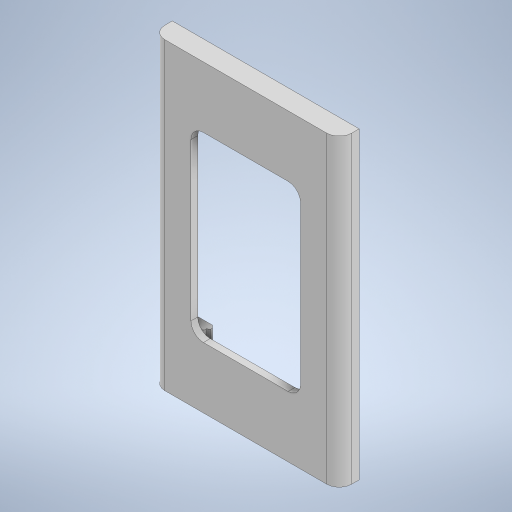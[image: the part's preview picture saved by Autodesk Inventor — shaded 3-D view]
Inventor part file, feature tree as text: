
AUTODESK INVENTOR PART (.ipt)
format: ipt  version: 2023 (Build 270158000, 158)  size: 365,056 bytes
history: native  units: mm
features: extrude x4, sketch x4, fillet x3, other x2, chamfer x2, mirror x2, shell x1
ambient origin geometry x8: Origin, YZ Plane, XZ Plane, XY Plane, X Axis, Y Axis, Z Axis, Center Point
bodies: Body1 (feature_tree)
feature tree (18):
  other  "솔리드1"
  extrude  "돌출1"  Depth=75.0mm
  fillet  "모깎기1"  Radius=122.0mm
  shell  "쉘1"  Thickness=44.0mm
  extrude  "돌출2"  Depth=73.0mm
  extrude  "돌출3"  Depth=8.0mm TaperAngle=0.0deg
  chamfer  "모따기1"  Distance=5.0mm
  extrude  "돌출4"  Depth=1.7mm
  mirror  "미러1"
  mirror  "미러2"
  sketch  "스케치5"
  fillet  "모깎기8"  Radius=8.0mm
  chamfer  "모따기3"  Distance=36.85mm
  other  "두껍게 하기2"
  fillet  "모깎기9"  Radius=6.9mm
  sketch  "스케치1"
  sketch  "스케치2"
  sketch  "스케치3"
